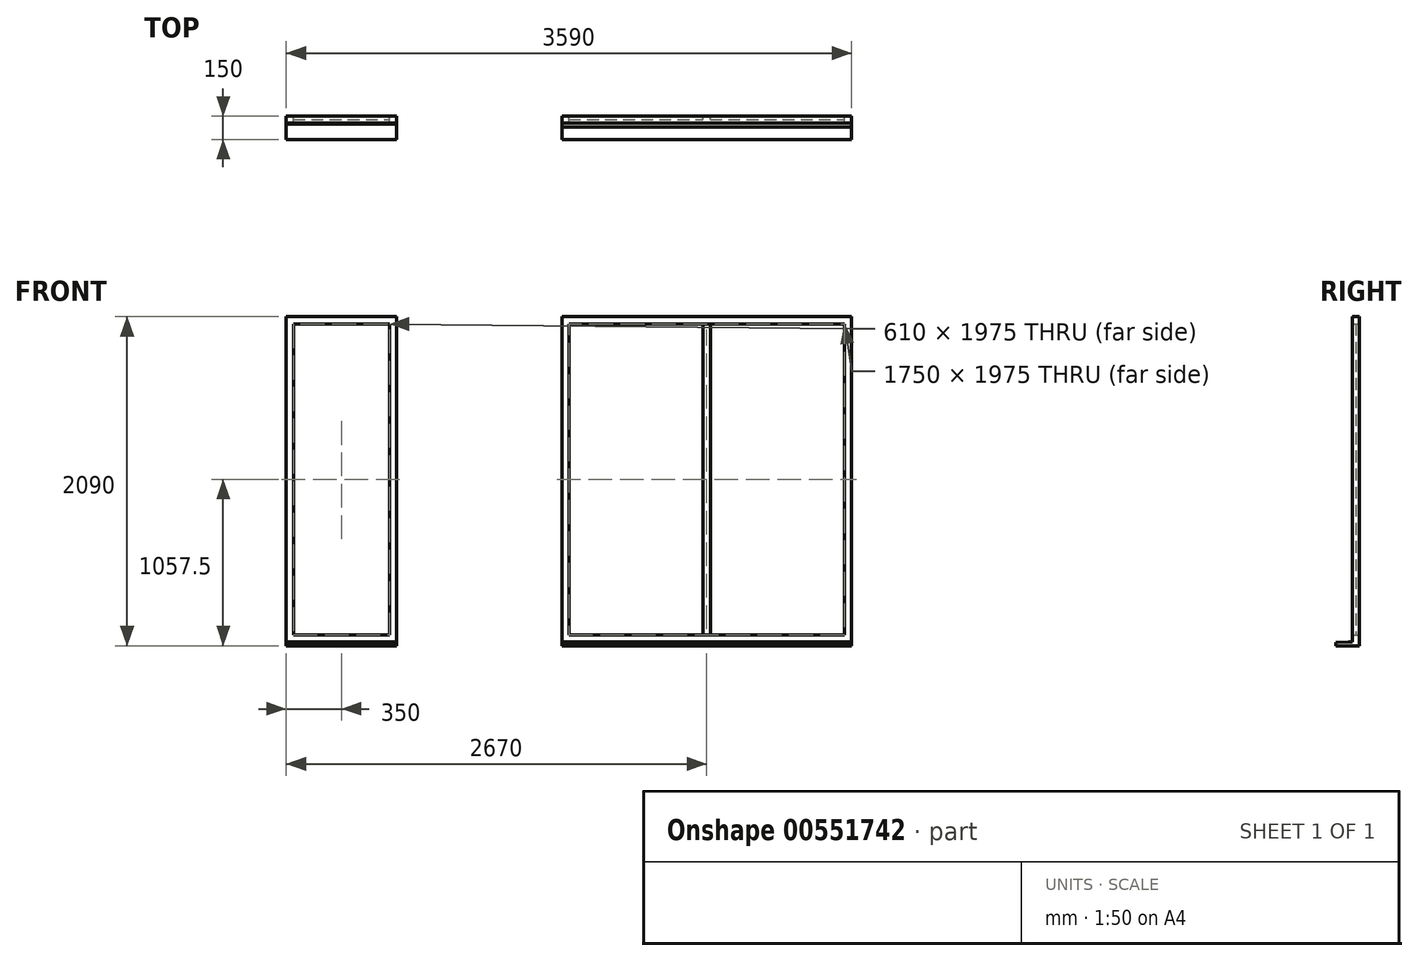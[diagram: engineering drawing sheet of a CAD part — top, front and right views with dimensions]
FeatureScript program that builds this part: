
annotation { "Feature Type Name" : "Feature", "Feature Type Description" : "" }
export const myFeature = defineFeature(function(context is Context, id is Id, definition is map)
    precondition{}
    {
        {
            var Q0;
            Q0=qCreatedBy(makeId("Front.planeOp"),FACE);
            var sketch = newSketch(context, id + "F0", { "sketchPlane" : qUnion([Q0])});
            skLineSegment(sketch, "E0.bottom", {"start": v(0, 0) * mm, "end": v(1840, 0) * mm});
            skLineSegment(sketch, "E0.top", {"start": v(0, 2090) * mm, "end": v(1840, 2090) * mm});
            skLineSegment(sketch, "E0.left", {"start": v(0, 0) * mm, "end": v(0, 2090) * mm});
            skLineSegment(sketch, "E0.right", {"start": v(1840, 0) * mm, "end": v(1840, 2090) * mm});
            skSolve(sketch);
        }
        {
            var Q0;
            Q0=qCreatedBy(makeId("Right.planeOp"),FACE);
            var sketch = newSketch(context, id + "F1", { "sketchPlane" : qUnion([Q0])});
            skLineSegment(sketch, "E1.bottom", {"start": v(0, 0) * mm, "end": v(-150, 0) * mm});
            skLineSegment(sketch, "E1.top", {"start": v(0, 25) * mm, "end": v(-150, 25) * mm});
            skLineSegment(sketch, "E1.left", {"start": v(0, 0) * mm, "end": v(0, 25) * mm});
            skLineSegment(sketch, "E1.right", {"start": v(-150, 0) * mm, "end": v(-150, 25) * mm});
            skSolve(sketch);
        }
        {
            var Q0;
            Q0 = qSketchRegion(id + "F1", true);
            extrude(context, id + "F2", {"entities" : qUnion([Q0]), "depth" : 1840 * mm, "offsetDistance" : 25 * mm});
        }
        {
            var Q0;
            Q0=qCreatedBy(makeId("Front.planeOp"),FACE);
            var sketch = newSketch(context, id + "F3", { "sketchPlane" : qUnion([Q0])});
            skLineSegment(sketch, "E2.bottom", {"start": v(45, 2045) * mm, "end": v(1795, 2045) * mm});
            skLineSegment(sketch, "E2.top", {"start": v(45, 70) * mm, "end": v(1795, 70) * mm});
            skLineSegment(sketch, "E2.left", {"start": v(45, 2045) * mm, "end": v(45, 70) * mm});
            skLineSegment(sketch, "E2.right", {"start": v(1795, 2045) * mm, "end": v(1795, 70) * mm});
            skLineSegment(sketch, "E3.bottom", {"start": v(897.5, 2045) * mm, "end": v(942.5, 2045) * mm});
            skLineSegment(sketch, "E3.top", {"start": v(897.5, 70) * mm, "end": v(942.5, 70) * mm});
            skLineSegment(sketch, "E3.left", {"start": v(897.5, 2045) * mm, "end": v(897.5, 70) * mm});
            skLineSegment(sketch, "E3.right", {"start": v(942.5, 2045) * mm, "end": v(942.5, 70) * mm});
            skPoint(sketch, "E4", {"position": v(920, 2045) * mm});
            skLineSegment(sketch, "E5.bottom", {"start": v(0, 2090) * mm, "end": v(1840, 2090) * mm});
            skLineSegment(sketch, "E5.top", {"start": v(0, 25) * mm, "end": v(1840, 25) * mm});
            skLineSegment(sketch, "E5.left", {"start": v(0, 2090) * mm, "end": v(0, 25) * mm});
            skLineSegment(sketch, "E5.right", {"start": v(1840, 2090) * mm, "end": v(1840, 25) * mm});
            skSolve(sketch);
        }
        {
            var Q0;
            Q0=makeQuery(id+"F3.imprint","IMPRINT",FACE,{"disambiguationData":[TD([[makeQuery(id+"F3.imprint","IMPRINT",EDGE,{"derivedFrom":sQuery(id+"F3.wireOp",EDGE,"E3.bottom")}),-1.0]])]});
            var Q1;
            {var subQ3=sQuery(id+"F3.wireOp",EDGE,"E2.left");Q1=makeQuery(id+"F3.imprint","IMPRINT",FACE,{"disambiguationData":[TD([[makeQuery(id+"F3.imprint","IMPRINT",EDGE,{"derivedFrom":subQ3}),-1.0]])]});}
            extrude(context, id + "F4", {"entities" : qUnion([Q0, Q1]), "operationType" : NewBodyOperationType.ADD, "depth" : 45 * mm, "offsetDistance" : 25 * mm});
        }
        {
            var Q0;
            {var subQ0=sQuery(id+"F3.wireOp",EDGE,"E2.left");Q0=makeQuery(id+"F3.imprint","IMPRINT",FACE,{"disambiguationData":[TD([[makeQuery(id+"F3.imprint","IMPRINT",EDGE,{"derivedFrom":subQ0}),1.0]])]});}
            var Q1;
            {var subQ0=sQuery(id+"F3.wireOp",EDGE,"E2.right");Q1=makeQuery(id+"F3.imprint","IMPRINT",FACE,{"disambiguationData":[TD([[makeQuery(id+"F3.imprint","IMPRINT",EDGE,{"derivedFrom":subQ0}),-1.0]])]});}
            extrude(context, id + "F5", {"entities" : qUnion([Q0, Q1]), "depth" : 22 * mm, "offsetDistance" : 25 * mm});
        }
        {
            var Q0;
            Q0=makeQuery(id+"F2.opExtrude","SWEPT_EDGE",EDGE,{"disambiguationData":[OSD([sQuery(id+"F1.wireOp",EDGE,"E1.top"),sQuery(id+"F1.wireOp",EDGE,"E1.right")])]});
            chamfer(context, id + "F6", {"entities" : qUnion([Q0]), "chamferType" : ChamferType.TWO_OFFSETS, "width1" : 5 * mm, "oppositeDirection" : false, "width2" : 80 * mm, "tangentPropagation" : true});
        }
        {
            var Q0;
            Q0=qCreatedBy(makeId("Right.planeOp"),FACE);
            cPlane(context, id + "F7", {"entities" : qUnion([Q0]), "cplaneType" : CPlaneType.OFFSET, "offset" : 1750 * mm, "oppositeDirection" : true, "width" : 150 * mm, "height" : 150 * mm});
        }
        {
            var Q0;
            Q0=qCreatedBy(id+"F7.planeOp",FACE);
            var sketch = newSketch(context, id + "F8", { "sketchPlane" : qUnion([Q0])});
            skLineSegment(sketch, "E6.bottom", {"start": v(0, 0) * mm, "end": v(-150, 0) * mm});
            skLineSegment(sketch, "E6.top", {"start": v(0, 25) * mm, "end": v(-150, 25) * mm});
            skLineSegment(sketch, "E6.left", {"start": v(0, 0) * mm, "end": v(0, 25) * mm});
            skLineSegment(sketch, "E6.right", {"start": v(-150, 0) * mm, "end": v(-150, 25) * mm});
            skSolve(sketch);
        }
        {
            var Q0;
            Q0 = qSketchRegion(id + "F8", true);
            extrude(context, id + "F9", {"entities" : qUnion([Q0]), "depth" : 700 * mm, "offsetDistance" : 25 * mm});
        }
        {
            var Q0;
            Q0=makeQuery(id+"F9.opExtrude","SWEPT_FACE",FACE,{"disambiguationData":[OSD([sQuery(id+"F8.wireOp",EDGE,"E6.left")])]});
            var sketch = newSketch(context, id + "F10", { "sketchPlane" : qUnion([Q0])});
            skLineSegment(sketch, "E7.bottom", {"start": v(1750, 25) * mm, "end": v(1050, 25) * mm});
            skLineSegment(sketch, "E7.top", {"start": v(1750, 2090) * mm, "end": v(1050, 2090) * mm});
            skLineSegment(sketch, "E7.left", {"start": v(1750, 25) * mm, "end": v(1750, 2090) * mm});
            skLineSegment(sketch, "E7.right", {"start": v(1050, 25) * mm, "end": v(1050, 2090) * mm});
            skLineSegment(sketch, "E8.bottom", {"start": v(1705, 2045) * mm, "end": v(1095, 2045) * mm});
            skLineSegment(sketch, "E8.top", {"start": v(1705, 70) * mm, "end": v(1095, 70) * mm});
            skLineSegment(sketch, "E8.left", {"start": v(1705, 2045) * mm, "end": v(1705, 70) * mm});
            skLineSegment(sketch, "E8.right", {"start": v(1095, 2045) * mm, "end": v(1095, 70) * mm});
            skSolve(sketch);
        }
        {
            var Q0;
            Q0=makeQuery(id+"F10.imprint","IMPRINT",FACE,{"disambiguationData":[TD([[makeQuery(id+"F10.imprint","IMPRINT",EDGE,{"derivedFrom":sQuery(id+"F10.wireOp",EDGE,"E7.bottom")}),1.0]])]});
            extrude(context, id + "F11", {"entities" : qUnion([Q0]), "operationType" : NewBodyOperationType.ADD, "oppositeDirection" : true, "depth" : 45 * mm, "offsetDistance" : 25 * mm});
        }
        {
            var Q0;
            Q0=makeQuery(id+"F10.imprint","IMPRINT",FACE,{"disambiguationData":[TD([[makeQuery(id+"F10.imprint","IMPRINT",EDGE,{"derivedFrom":sQuery(id+"F10.wireOp",EDGE,"E8.bottom")}),1.0]])]});
            extrude(context, id + "F12", {"entities" : qUnion([Q0]), "oppositeDirection" : true, "depth" : 22 * mm, "offsetDistance" : 25 * mm});
        }
        {
            var Q0;
            Q0=makeQuery(id+"F9.opExtrude","SWEPT_EDGE",EDGE,{"disambiguationData":[OSD([sQuery(id+"F8.wireOp",EDGE,"E6.top"),sQuery(id+"F8.wireOp",EDGE,"E6.right")])]});
            chamfer(context, id + "F13", {"entities" : qUnion([Q0]), "chamferType" : ChamferType.TWO_OFFSETS, "width1" : 5 * mm, "oppositeDirection" : false, "width2" : 100 * mm, "tangentPropagation" : true});
        }
    });
